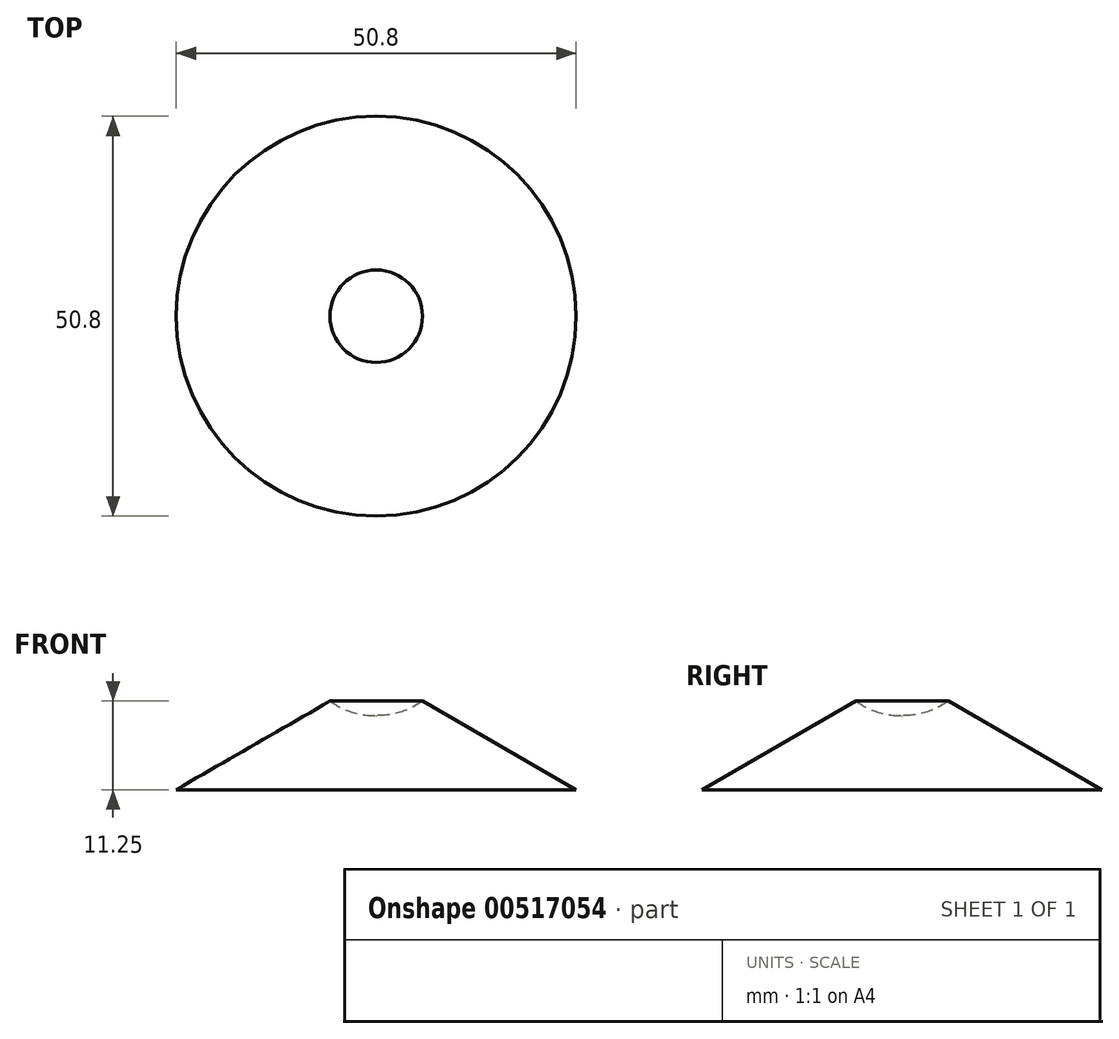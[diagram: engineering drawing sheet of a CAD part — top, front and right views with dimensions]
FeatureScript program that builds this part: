
annotation { "Feature Type Name" : "Feature", "Feature Type Description" : "" }
export const myFeature = defineFeature(function(context is Context, id is Id, definition is map)
    precondition{}
    {
        {
            var Q0;
            Q0=qCreatedBy(makeId("Front.planeOp"),FACE);
            var sketch = newSketch(context, id + "F0", { "sketchPlane" : qUnion([Q0])});
            skLineSegment(sketch, "E0", {"start": v(0, 0) * mm, "end": v(25.4, 0) * mm});
            skLineSegment(sketch, "E1", {"start": v(25.4, 0) * mm, "end": v(5.56, 11.43) * mm});
            skLineSegment(sketch, "E2", {"start": v(5.56, 11.43) * mm, "end": v(0, 11.43) * mm});
            skLineSegment(sketch, "E3", {"start": v(0, 0) * mm, "end": v(0, 11.43) * mm});
            skSolve(sketch);
        }
        {
            var Q0;
            Q0=makeQuery(id+"F0.imprint","IMPRINT",FACE,{"disambiguationData":[TD([[makeQuery(id+"F0.imprint","IMPRINT",EDGE,{"derivedFrom":sQuery(id+"F0.wireOp",EDGE,"E0")}),1.0]])]});
            var Q1;
            Q1 = qSketchRegion(id + "F2", true);
            var Q2;
            Q2=sQuery(id+"F0.wireOp",EDGE,"E2");
            var Q3;
            Q3=sQuery(id+"F0.wireOp",EDGE,"E0");
            var Q4;
            Q4=sQuery(id+"F0.wireOp",EDGE,"E1");
            var Q5;
            Q5=sQuery(id+"F0.wireOp",EDGE,"E3");
            revolve(context, id + "F1", {"entities" : qUnion([Q0, Q1]), "surfaceEntities" : qUnion([Q2, Q3, Q4]), "axis" : qUnion([Q5]), "revolveType" : RevolveType.FULL});
        }
        {
            var Q0;
            Q0=qCreatedBy(makeId("Front.planeOp"),FACE);
            var sketch = newSketch(context, id + "F2", { "sketchPlane" : qUnion([Q0])});
            skCircle(sketch, "E4", {"center": v(-0.03, 19.56) * mm, "radius": 10.16 * mm});
            skPoint(sketch, "E4.first.point", {"position": v(-8.7, 14.25) * mm});
            skPoint(sketch, "E4.second.point", {"position": v(8.63, 14.25) * mm});
            skPoint(sketch, "E4.third.point", {"position": v(5.15, 28.3) * mm});
            skLineSegment(sketch, "E5", {"start": v(0, -21.64) * mm, "end": v(0, 56.53) * mm});
            skSolve(sketch);
        }
        {
            var Q0;
            {var subQ0=sQuery(id+"F2.wireOp",EDGE,"E5");var subQ1=sQuery(id+"F2.wireOp",EDGE,"E4");var subQ2=makeQuery(id+"F2.imprint","INTERSECT",VERTEX,{"disambiguationData":[OD(0.0)],"derivedFrom":[subQ1,subQ0]});Q0=makeQuery(id+"F2.imprint","IMPRINT",FACE,{"disambiguationData":[TD([[makeQuery(id+"F2.imprint","IMPRINT",EDGE,{"disambiguationData":[TD([[subQ2,1.0]])],"derivedFrom":subQ1}),1.0]])]});}
            var Q1;
            Q1=sQuery(id+"F2.wireOp",EDGE,"E4");
            var Q2;
            Q2=sQuery(id+"F2.wireOp",EDGE,"E5");
            var Q3;
            Q3=sQuery(id+"F2.wireOp",EDGE,"E5");
            revolve(context, id + "F3", {"operationType" : NewBodyOperationType.ADD, "entities" : qUnion([Q0]), "surfaceEntities" : qUnion([Q1, Q2]), "axis" : qUnion([Q3]), "revolveType" : RevolveType.FULL});
        }
    });
